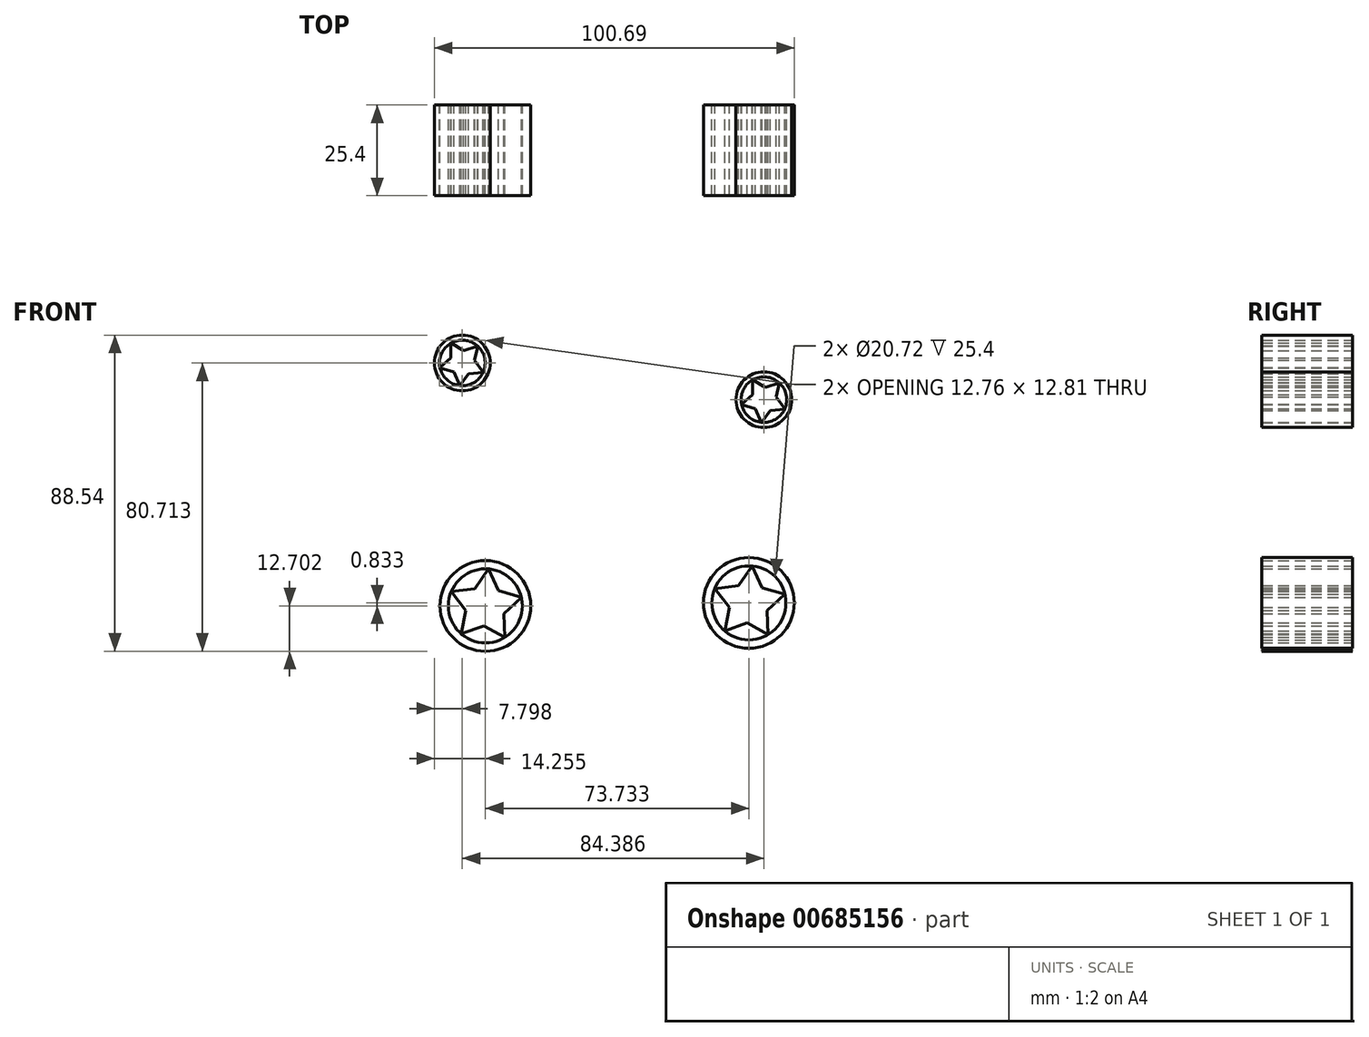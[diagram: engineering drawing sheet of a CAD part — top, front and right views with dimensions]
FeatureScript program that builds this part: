
annotation { "Feature Type Name" : "Feature", "Feature Type Description" : "" }
export const myFeature = defineFeature(function(context is Context, id is Id, definition is map)
    precondition{}
    {
        {
            var Q0;
            Q0=qCreatedBy(makeId("Front.planeOp"),FACE);
            var sketch = newSketch(context, id + "F0", { "sketchPlane" : qUnion([Q0])});
            skCircle(sketch, "E0", {"center": v(-47.02, 42.67) * mm, "radius": 6.39 * mm});
            skLineSegment(sketch, "E1", {"start": v(-53.35, 41.36) * mm, "end": v(-50.2, 44.1) * mm});
            skLineSegment(sketch, "E2", {"start": v(-53.35, 41.36) * mm, "end": v(-49.37, 40.1) * mm});
            skLineSegment(sketch, "E3", {"start": v(-47.73, 36.25) * mm, "end": v(-49.37, 40.1) * mm});
            skLineSegment(sketch, "E4", {"start": v(-47.73, 36.25) * mm, "end": v(-45.3, 39.65) * mm});
            skLineSegment(sketch, "E5", {"start": v(-41.13, 40.02) * mm, "end": v(-45.3, 39.65) * mm});
            skLineSegment(sketch, "E6", {"start": v(-41.13, 40.02) * mm, "end": v(-43.6, 43.38) * mm});
            skLineSegment(sketch, "E7", {"start": v(-42.67, 47.46) * mm, "end": v(-43.6, 43.38) * mm});
            skLineSegment(sketch, "E8", {"start": v(-42.67, 47.46) * mm, "end": v(-46.64, 46.14) * mm});
            skLineSegment(sketch, "E9", {"start": v(-50.23, 48.29) * mm, "end": v(-50.2, 44.1) * mm});
            skLineSegment(sketch, "E10", {"start": v(-50.23, 48.29) * mm, "end": v(-46.64, 46.14) * mm});
            skCircle(sketch, "E11", {"center": v(-47.02, 42.67) * mm, "radius": 7.8 * mm});
            skCircle(sketch, "E12", {"center": v(37.36, 32.4) * mm, "radius": 6.39 * mm});
            skLineSegment(sketch, "E13", {"start": v(31.04, 31.08) * mm, "end": v(34.19, 33.82) * mm});
            skLineSegment(sketch, "E14", {"start": v(31.04, 31.08) * mm, "end": v(35.02, 29.81) * mm});
            skLineSegment(sketch, "E15", {"start": v(36.66, 25.97) * mm, "end": v(35.02, 29.81) * mm});
            skLineSegment(sketch, "E16", {"start": v(36.66, 25.97) * mm, "end": v(39.1, 29.36) * mm});
            skLineSegment(sketch, "E17", {"start": v(43.26, 29.73) * mm, "end": v(39.1, 29.36) * mm});
            skLineSegment(sketch, "E18", {"start": v(43.26, 29.73) * mm, "end": v(40.78, 33.1) * mm});
            skLineSegment(sketch, "E19", {"start": v(41.71, 37.17) * mm, "end": v(40.78, 33.1) * mm});
            skLineSegment(sketch, "E20", {"start": v(41.71, 37.17) * mm, "end": v(37.75, 35.86) * mm});
            skLineSegment(sketch, "E21", {"start": v(34.16, 38) * mm, "end": v(34.19, 33.82) * mm});
            skLineSegment(sketch, "E22", {"start": v(34.16, 38) * mm, "end": v(37.75, 35.86) * mm});
            skCircle(sketch, "E23", {"center": v(37.36, 32.4) * mm, "radius": 7.8 * mm});
            skCircle(sketch, "E24", {"center": v(-47.02, 42.67) * mm, "radius": 3.49 * mm});
            skCircle(sketch, "E25", {"center": v(37.36, 32.4) * mm, "radius": 3.49 * mm});
            skCircle(sketch, "E26", {"center": v(-40.57, -25.36) * mm, "radius": 12.7 * mm});
            skCircle(sketch, "E27", {"center": v(-40.57, -25.36) * mm, "radius": 10.36 * mm});
            skCircle(sketch, "E28.cCircle", {"center": v(-40.57, -25.36) * mm, "radius": 10.36 * mm, "construction": true});
            skLineSegment(sketch, "E29", {"start": v(-36.92, -21.13) * mm, "end": v(-30.48, -22.99) * mm});
            skLineSegment(sketch, "E30", {"start": v(-36.92, -21.13) * mm, "end": v(-39.7, -15.03) * mm});
            skLineSegment(sketch, "E31", {"start": v(-30.48, -22.99) * mm, "end": v(-35.41, -27.52) * mm});
            skLineSegment(sketch, "E32", {"start": v(-35.2, -34.22) * mm, "end": v(-35.41, -27.52) * mm});
            skLineSegment(sketch, "E33", {"start": v(-35.2, -34.22) * mm, "end": v(-41.03, -30.93) * mm});
            skLineSegment(sketch, "E34", {"start": v(-47.33, -33.2) * mm, "end": v(-41.03, -30.93) * mm});
            skLineSegment(sketch, "E35", {"start": v(-47.33, -33.2) * mm, "end": v(-46, -26.64) * mm});
            skLineSegment(sketch, "E36", {"start": v(-50.12, -21.35) * mm, "end": v(-46, -26.64) * mm});
            skLineSegment(sketch, "E37", {"start": v(-50.12, -21.35) * mm, "end": v(-43.46, -20.58) * mm});
            skLineSegment(sketch, "E38", {"start": v(-39.7, -15.03) * mm, "end": v(-43.46, -20.58) * mm});
            skCircle(sketch, "E39", {"center": v(33.17, -24.53) * mm, "radius": 12.7 * mm});
            skCircle(sketch, "E40", {"center": v(33.17, -24.53) * mm, "radius": 10.36 * mm});
            skCircle(sketch, "E41.cCircle", {"center": v(33.17, -24.53) * mm, "radius": 10.36 * mm, "construction": true});
            skLineSegment(sketch, "E42", {"start": v(36.82, -20.3) * mm, "end": v(43.25, -22.16) * mm});
            skLineSegment(sketch, "E43", {"start": v(36.82, -20.3) * mm, "end": v(34.03, -14.2) * mm});
            skLineSegment(sketch, "E44", {"start": v(43.25, -22.16) * mm, "end": v(38.32, -26.69) * mm});
            skLineSegment(sketch, "E45", {"start": v(38.54, -33.39) * mm, "end": v(38.32, -26.69) * mm});
            skLineSegment(sketch, "E46", {"start": v(38.54, -33.39) * mm, "end": v(32.7, -30.1) * mm});
            skLineSegment(sketch, "E47", {"start": v(26.4, -32.37) * mm, "end": v(32.7, -30.1) * mm});
            skLineSegment(sketch, "E48", {"start": v(26.4, -32.37) * mm, "end": v(27.73, -25.8) * mm});
            skLineSegment(sketch, "E49", {"start": v(23.61, -20.51) * mm, "end": v(27.73, -25.8) * mm});
            skLineSegment(sketch, "E50", {"start": v(23.61, -20.51) * mm, "end": v(30.27, -19.75) * mm});
            skLineSegment(sketch, "E51", {"start": v(34.03, -14.2) * mm, "end": v(30.27, -19.75) * mm});
            skSolve(sketch);
        }
        {
            var Q0;
            Q0=makeQuery(id+"F0.imprint","IMPRINT",FACE,{"disambiguationData":[TD([[makeQuery(id+"F0.imprint","IMPRINT",EDGE,{"derivedFrom":sQuery(id+"F0.wireOp",EDGE,"E11")}),1.0]])]});
            var Q1;
            {var subQ0=sQuery(id+"F0.wireOp",EDGE,"E5");var subQ1=sQuery(id+"F0.wireOp",EDGE,"E0");var subQ2=makeQuery(id+"F0.imprint","INTERSECT",VERTEX,{"derivedFrom":[subQ1,subQ0]});Q1=makeQuery(id+"F0.imprint","IMPRINT",FACE,{"disambiguationData":[TD([[makeQuery(id+"F0.imprint","IMPRINT",EDGE,{"disambiguationData":[TD([[subQ2,-1.0]])],"derivedFrom":subQ1}),1.0]])]});}
            var Q2;
            {var subQ0=sQuery(id+"F0.wireOp",EDGE,"E24");var subQ5=makeQuery(id+"F0.imprint","INTERSECT",VERTEX,{"derivedFrom":[sQuery(id+"F0.wireOp",EDGE,"E6"),sQuery(id+"F0.wireOp",EDGE,"E7"),subQ0]});Q2=makeQuery(id+"F0.imprint","IMPRINT",FACE,{"disambiguationData":[TD([[makeQuery(id+"F0.imprint","IMPRINT",EDGE,{"disambiguationData":[TD([[subQ5,-1.0]])],"derivedFrom":subQ0}),1.0]])]});}
            var Q3;
            {var subQ0=sQuery(id+"F0.wireOp",EDGE,"E3");var subQ1=sQuery(id+"F0.wireOp",EDGE,"E0");var subQ2=makeQuery(id+"F0.imprint","INTERSECT",VERTEX,{"derivedFrom":[subQ1,subQ0]});Q3=makeQuery(id+"F0.imprint","IMPRINT",FACE,{"disambiguationData":[TD([[makeQuery(id+"F0.imprint","IMPRINT",EDGE,{"disambiguationData":[TD([[subQ2,-1.0]])],"derivedFrom":subQ1}),1.0]])]});}
            var Q4;
            {var subQ0=sQuery(id+"F0.wireOp",EDGE,"E1");var subQ1=sQuery(id+"F0.wireOp",EDGE,"E0");var subQ2=makeQuery(id+"F0.imprint","INTERSECT",VERTEX,{"derivedFrom":[subQ1,subQ0]});Q4=makeQuery(id+"F0.imprint","IMPRINT",FACE,{"disambiguationData":[TD([[makeQuery(id+"F0.imprint","IMPRINT",EDGE,{"disambiguationData":[TD([[subQ2,-1.0]])],"derivedFrom":subQ1}),1.0]])]});}
            var Q5;
            {var subQ0=sQuery(id+"F0.wireOp",EDGE,"E10");var subQ1=sQuery(id+"F0.wireOp",EDGE,"E0");var subQ2=makeQuery(id+"F0.imprint","INTERSECT",VERTEX,{"derivedFrom":[subQ1,subQ0]});Q5=makeQuery(id+"F0.imprint","IMPRINT",FACE,{"disambiguationData":[TD([[makeQuery(id+"F0.imprint","IMPRINT",EDGE,{"disambiguationData":[TD([[subQ2,-1.0]])],"derivedFrom":subQ1}),1.0]])]});}
            var Q6;
            {var subQ0=sQuery(id+"F0.wireOp",EDGE,"E8");var subQ1=sQuery(id+"F0.wireOp",EDGE,"E0");var subQ2=makeQuery(id+"F0.imprint","INTERSECT",VERTEX,{"derivedFrom":[subQ1,subQ0]});Q6=makeQuery(id+"F0.imprint","IMPRINT",FACE,{"disambiguationData":[TD([[makeQuery(id+"F0.imprint","IMPRINT",EDGE,{"disambiguationData":[TD([[subQ2,1.0]])],"derivedFrom":subQ1}),1.0]])]});}
            var Q7;
            {var subQ0=sQuery(id+"F0.wireOp",EDGE,"E17");var subQ1=sQuery(id+"F0.wireOp",EDGE,"E12");var subQ2=makeQuery(id+"F0.imprint","INTERSECT",VERTEX,{"derivedFrom":[subQ1,subQ0]});Q7=makeQuery(id+"F0.imprint","IMPRINT",FACE,{"disambiguationData":[TD([[makeQuery(id+"F0.imprint","IMPRINT",EDGE,{"disambiguationData":[TD([[subQ2,-1.0]])],"derivedFrom":subQ1}),1.0]])]});}
            var Q8;
            Q8=makeQuery(id+"F0.imprint","IMPRINT",FACE,{"disambiguationData":[TD([[makeQuery(id+"F0.imprint","IMPRINT",EDGE,{"derivedFrom":sQuery(id+"F0.wireOp",EDGE,"E23")}),1.0]])]});
            var Q9;
            {var subQ0=sQuery(id+"F0.wireOp",EDGE,"E15");var subQ1=sQuery(id+"F0.wireOp",EDGE,"E12");var subQ2=makeQuery(id+"F0.imprint","INTERSECT",VERTEX,{"derivedFrom":[subQ1,subQ0]});Q9=makeQuery(id+"F0.imprint","IMPRINT",FACE,{"disambiguationData":[TD([[makeQuery(id+"F0.imprint","IMPRINT",EDGE,{"disambiguationData":[TD([[subQ2,-1.0]])],"derivedFrom":subQ1}),1.0]])]});}
            var Q10;
            {var subQ0=sQuery(id+"F0.wireOp",EDGE,"E25");var subQ5=makeQuery(id+"F0.imprint","INTERSECT",VERTEX,{"derivedFrom":[sQuery(id+"F0.wireOp",EDGE,"E18"),sQuery(id+"F0.wireOp",EDGE,"E19"),subQ0]});Q10=makeQuery(id+"F0.imprint","IMPRINT",FACE,{"disambiguationData":[TD([[makeQuery(id+"F0.imprint","IMPRINT",EDGE,{"disambiguationData":[TD([[subQ5,-1.0]])],"derivedFrom":subQ0}),1.0]])]});}
            var Q11;
            {var subQ0=sQuery(id+"F0.wireOp",EDGE,"E13");var subQ1=sQuery(id+"F0.wireOp",EDGE,"E12");var subQ2=makeQuery(id+"F0.imprint","INTERSECT",VERTEX,{"derivedFrom":[subQ1,subQ0]});Q11=makeQuery(id+"F0.imprint","IMPRINT",FACE,{"disambiguationData":[TD([[makeQuery(id+"F0.imprint","IMPRINT",EDGE,{"disambiguationData":[TD([[subQ2,-1.0]])],"derivedFrom":subQ1}),1.0]])]});}
            var Q12;
            {var subQ0=sQuery(id+"F0.wireOp",EDGE,"E22");var subQ1=sQuery(id+"F0.wireOp",EDGE,"E12");var subQ2=makeQuery(id+"F0.imprint","INTERSECT",VERTEX,{"derivedFrom":[subQ1,subQ0]});Q12=makeQuery(id+"F0.imprint","IMPRINT",FACE,{"disambiguationData":[TD([[makeQuery(id+"F0.imprint","IMPRINT",EDGE,{"disambiguationData":[TD([[subQ2,-1.0]])],"derivedFrom":subQ1}),1.0]])]});}
            var Q13;
            {var subQ0=sQuery(id+"F0.wireOp",EDGE,"E20");var subQ1=sQuery(id+"F0.wireOp",EDGE,"E12");var subQ2=makeQuery(id+"F0.imprint","INTERSECT",VERTEX,{"derivedFrom":[subQ1,subQ0]});Q13=makeQuery(id+"F0.imprint","IMPRINT",FACE,{"disambiguationData":[TD([[makeQuery(id+"F0.imprint","IMPRINT",EDGE,{"disambiguationData":[TD([[subQ2,1.0]])],"derivedFrom":subQ1}),1.0]])]});}
            var Q14;
            Q14=makeQuery(id+"F0.imprint","IMPRINT",FACE,{"disambiguationData":[TD([[makeQuery(id+"F0.imprint","IMPRINT",EDGE,{"derivedFrom":sQuery(id+"F0.wireOp",EDGE,"E26")}),1.0]])]});
            var Q15;
            Q15=makeQuery(id+"F0.imprint","IMPRINT",FACE,{"disambiguationData":[TD([[makeQuery(id+"F0.imprint","IMPRINT",EDGE,{"derivedFrom":sQuery(id+"F0.wireOp",EDGE,"E29")}),-1.0]])]});
            var Q16;
            Q16=makeQuery(id+"F0.imprint","IMPRINT",FACE,{"disambiguationData":[TD([[makeQuery(id+"F0.imprint","IMPRINT",EDGE,{"derivedFrom":sQuery(id+"F0.wireOp",EDGE,"E39")}),1.0]])]});
            var Q17;
            Q17=makeQuery(id+"F0.imprint","IMPRINT",FACE,{"disambiguationData":[TD([[makeQuery(id+"F0.imprint","IMPRINT",EDGE,{"derivedFrom":sQuery(id+"F0.wireOp",EDGE,"E42")}),-1.0]])]});
            extrude(context, id + "F1", {"entities" : qUnion([Q0, Q1, Q2, Q3, Q4, Q5, Q6, Q7, Q8, Q9, Q10, Q11, Q12, Q13, Q14, Q15, Q16, Q17]), "depth" : 25.4 * mm, "offsetDistance" : 25.4 * mm});
        }
    });
